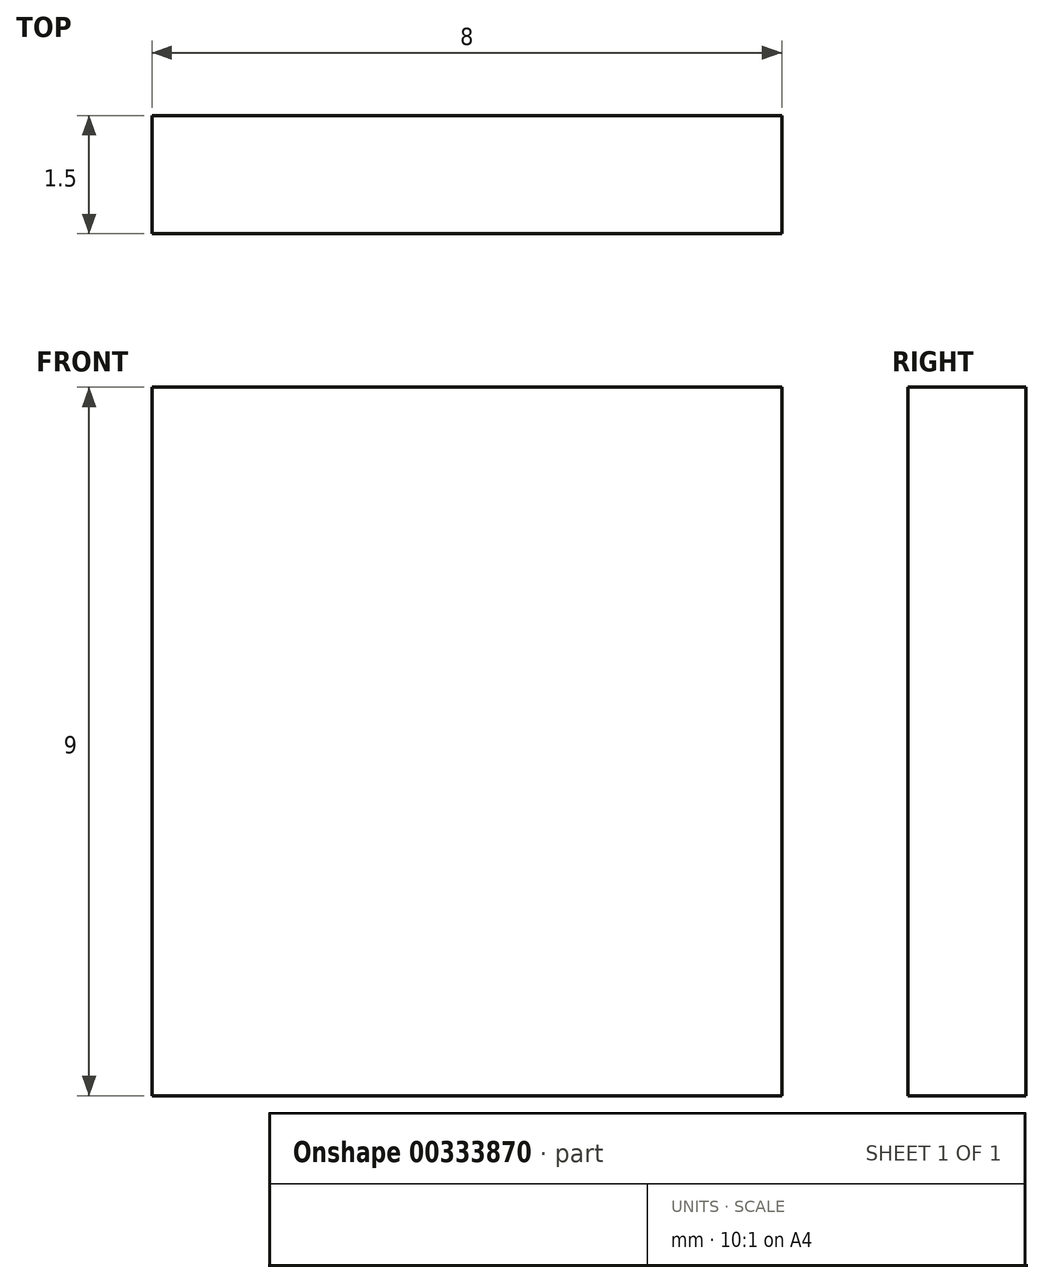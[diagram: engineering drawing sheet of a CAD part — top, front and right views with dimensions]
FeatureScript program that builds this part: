
annotation { "Feature Type Name" : "Feature", "Feature Type Description" : "" }
export const myFeature = defineFeature(function(context is Context, id is Id, definition is map)
    precondition{}
    {
        {
            var Q0;
            Q0=qCreatedBy(makeId("Front.planeOp"),FACE);
            var sketch = newSketch(context, id + "F0", { "sketchPlane" : qUnion([Q0])});
            skLineSegment(sketch, "E0.bottom", {"start": v(0, 0) * mm, "end": v(8, 0) * mm});
            skLineSegment(sketch, "E0.top", {"start": v(0, 9) * mm, "end": v(8, 9) * mm});
            skLineSegment(sketch, "E0.left", {"start": v(0, 0) * mm, "end": v(0, 9) * mm});
            skLineSegment(sketch, "E0.right", {"start": v(8, 0) * mm, "end": v(8, 9) * mm});
            skSolve(sketch);
        }
        {
            var Q0;
            Q0 = qSketchRegion(id + "F0", true);
            extrude(context, id + "F1", {"entities" : qUnion([Q0]), "depth" : 1.5 * mm});
        }
    });
